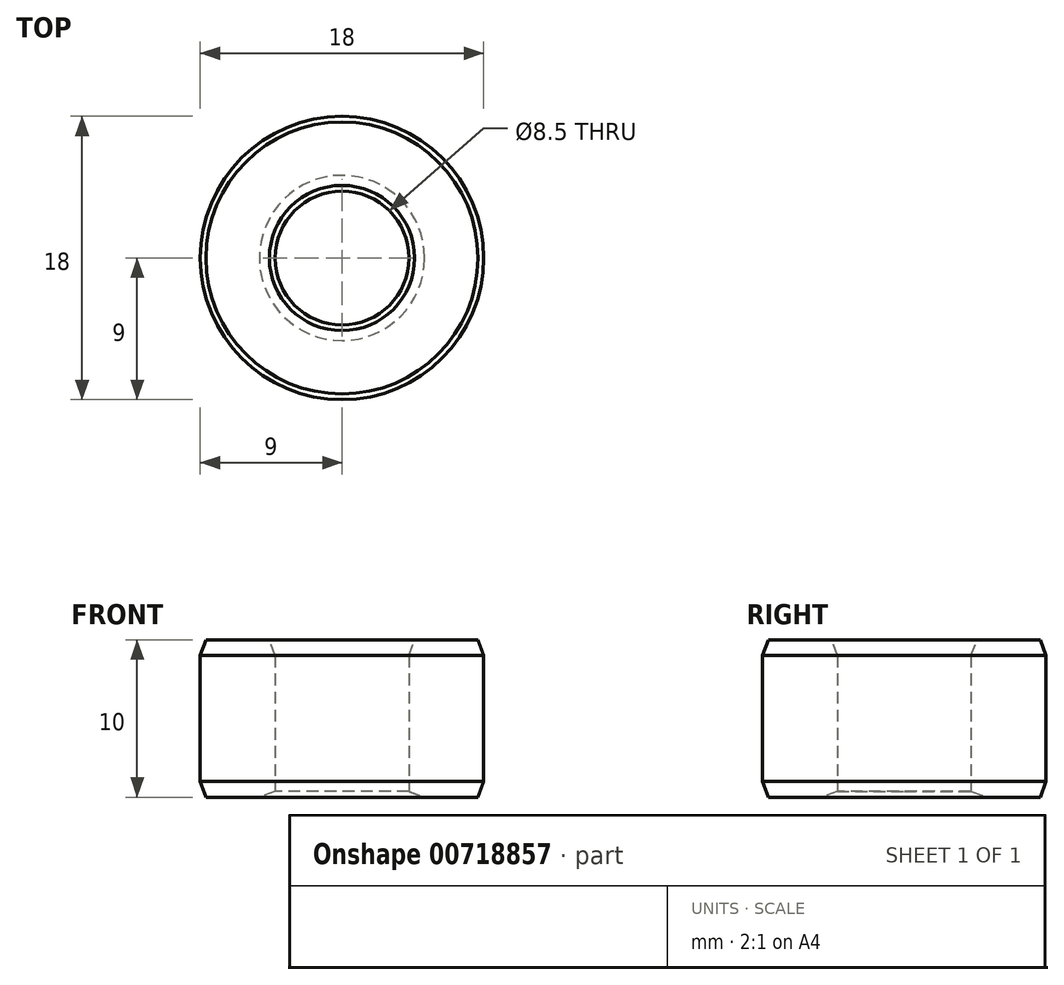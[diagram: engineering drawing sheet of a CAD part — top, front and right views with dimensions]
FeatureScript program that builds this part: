
annotation { "Feature Type Name" : "Feature", "Feature Type Description" : "" }
export const myFeature = defineFeature(function(context is Context, id is Id, definition is map)
    precondition{}
    {
        {
            var Q0;
            Q0=qCreatedBy(makeId("Top.planeOp"),FACE);
            var sketch = newSketch(context, id + "F0", { "sketchPlane" : qUnion([Q0])});
            skCircle(sketch, "E0", {"center": v(0, 0) * mm, "radius": 4.25 * mm});
            skCircle(sketch, "E1", {"center": v(0, 0) * mm, "radius": 9 * mm});
            skSolve(sketch);
        }
        {
            var Q0;
            Q0=makeQuery(id+"F0.imprint","IMPRINT",FACE,{"disambiguationData":[TD([[makeQuery(id+"F0.imprint","IMPRINT",EDGE,{"derivedFrom":sQuery(id+"F0.wireOp",EDGE,"E0")}),-1.0]])]});
            extrude(context, id + "F1", {"entities" : qUnion([Q0]), "depth" : 10 * mm, "offsetDistance" : 25 * mm});
        }
        {
            var Q0;
            Q0=makeQuery(id+"F1.opExtrude","CAP_EDGE",EDGE,{"disambiguationData":[OSD([sQuery(id+"F0.wireOp",EDGE,"E0")])],"isStart":false});
            chamfer(context, id + "F2", {"entities" : qUnion([Q0]), "chamferType" : ChamferType.OFFSET_ANGLE, "width" : 1 * mm, "oppositeDirection" : false, "angle" : 20 * degree, "tangentPropagation" : true});
        }
        {
            var Q0;
            Q0=makeQuery(id+"F1.opExtrude","CAP_EDGE",EDGE,{"disambiguationData":[OSD([sQuery(id+"F0.wireOp",EDGE,"E1")])],"isStart":false});
            chamfer(context, id + "F3", {"entities" : qUnion([Q0]), "chamferType" : ChamferType.OFFSET_ANGLE, "width" : 1 * mm, "oppositeDirection" : true, "angle" : 20 * degree, "tangentPropagation" : true});
        }
        {
            var Q0;
            Q0=makeQuery(id+"F1.opExtrude","CAP_EDGE",EDGE,{"disambiguationData":[OSD([sQuery(id+"F0.wireOp",EDGE,"E1")])],"isStart":true});
            chamfer(context, id + "F4", {"entities" : qUnion([Q0]), "chamferType" : ChamferType.OFFSET_ANGLE, "width" : 1 * mm, "oppositeDirection" : false, "angle" : 20 * degree, "tangentPropagation" : true});
        }
        {
            var Q0;
            Q0=makeQuery(id+"F1.opExtrude","CAP_EDGE",EDGE,{"disambiguationData":[OSD([sQuery(id+"F0.wireOp",EDGE,"E0")])],"isStart":true});
            chamfer(context, id + "F5", {"entities" : qUnion([Q0]), "chamferType" : ChamferType.OFFSET_ANGLE, "width" : 1 * mm, "oppositeDirection" : false, "angle" : 20 * degree, "tangentPropagation" : true});
        }
    });
